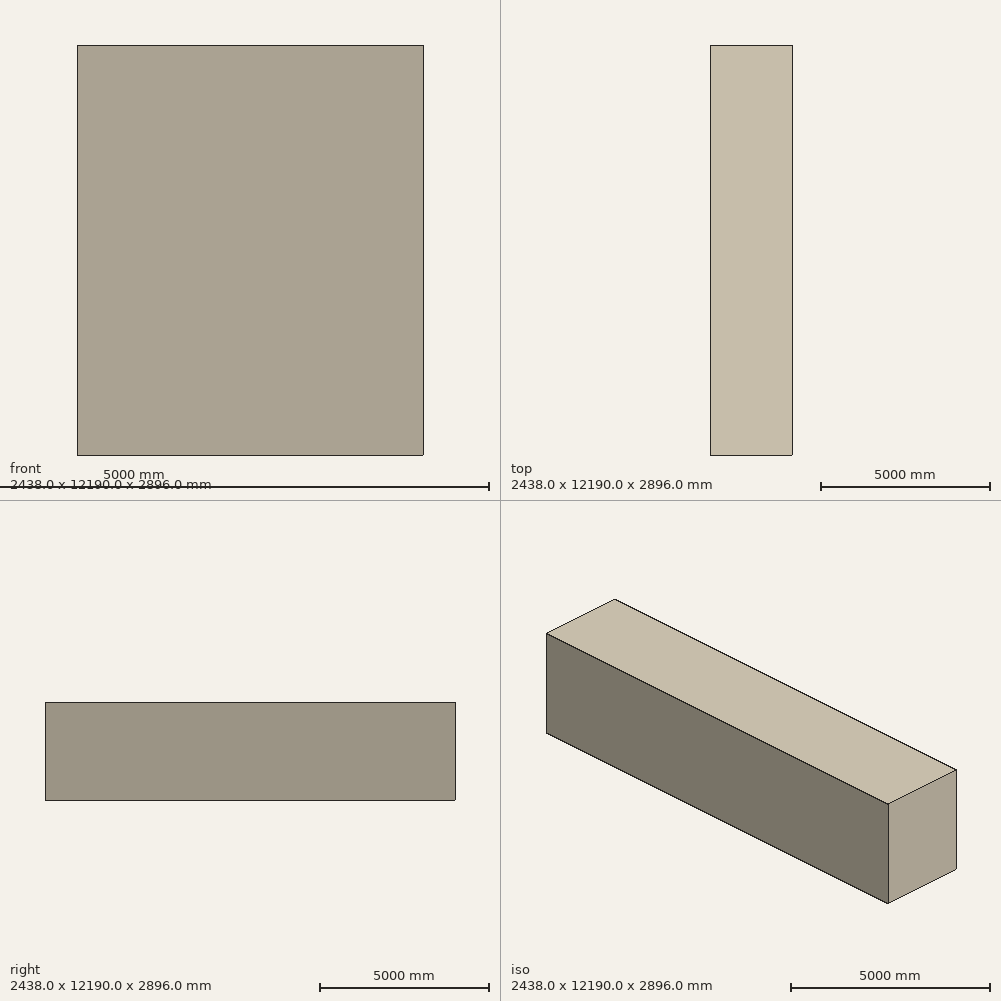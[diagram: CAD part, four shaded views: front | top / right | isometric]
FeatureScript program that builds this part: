
annotation { "Feature Type Name" : "Feature", "Feature Type Description" : "" }
export const myFeature = defineFeature(function(context is Context, id is Id, definition is map)
    precondition{}
    {
        {
            var Q0;
            Q0=qCreatedBy(makeId("Front.planeOp"),FACE);
            var sketch = newSketch(context, id + "F0", { "sketchPlane" : qUnion([Q0])});
            skLineSegment(sketch, "E0.bottom", {"start": v(-1219, 1448) * mm, "end": v(1219, 1448) * mm});
            skLineSegment(sketch, "E0.top", {"start": v(-1219, -1448) * mm, "end": v(1219, -1448) * mm});
            skLineSegment(sketch, "E0.left", {"start": v(-1219, 1448) * mm, "end": v(-1219, -1448) * mm});
            skLineSegment(sketch, "E0.right", {"start": v(1219, 1448) * mm, "end": v(1219, -1448) * mm});
            skPoint(sketch, "E0.middle", {"position": v(0, 0) * mm});
            skSolve(sketch);
        }
        {
            var Q0;
            Q0 = qSketchRegion(id + "F0", true);
            extrude(context, id + "F1", {"entities" : qUnion([Q0]), "depth" : 6095 * mm, "offsetDistance" : 25 * mm, "hasSecondDirection" : true, "secondDirectionOppositeDirection" : true, "secondDirectionDepth" : 6095 * mm});
        }
    });
